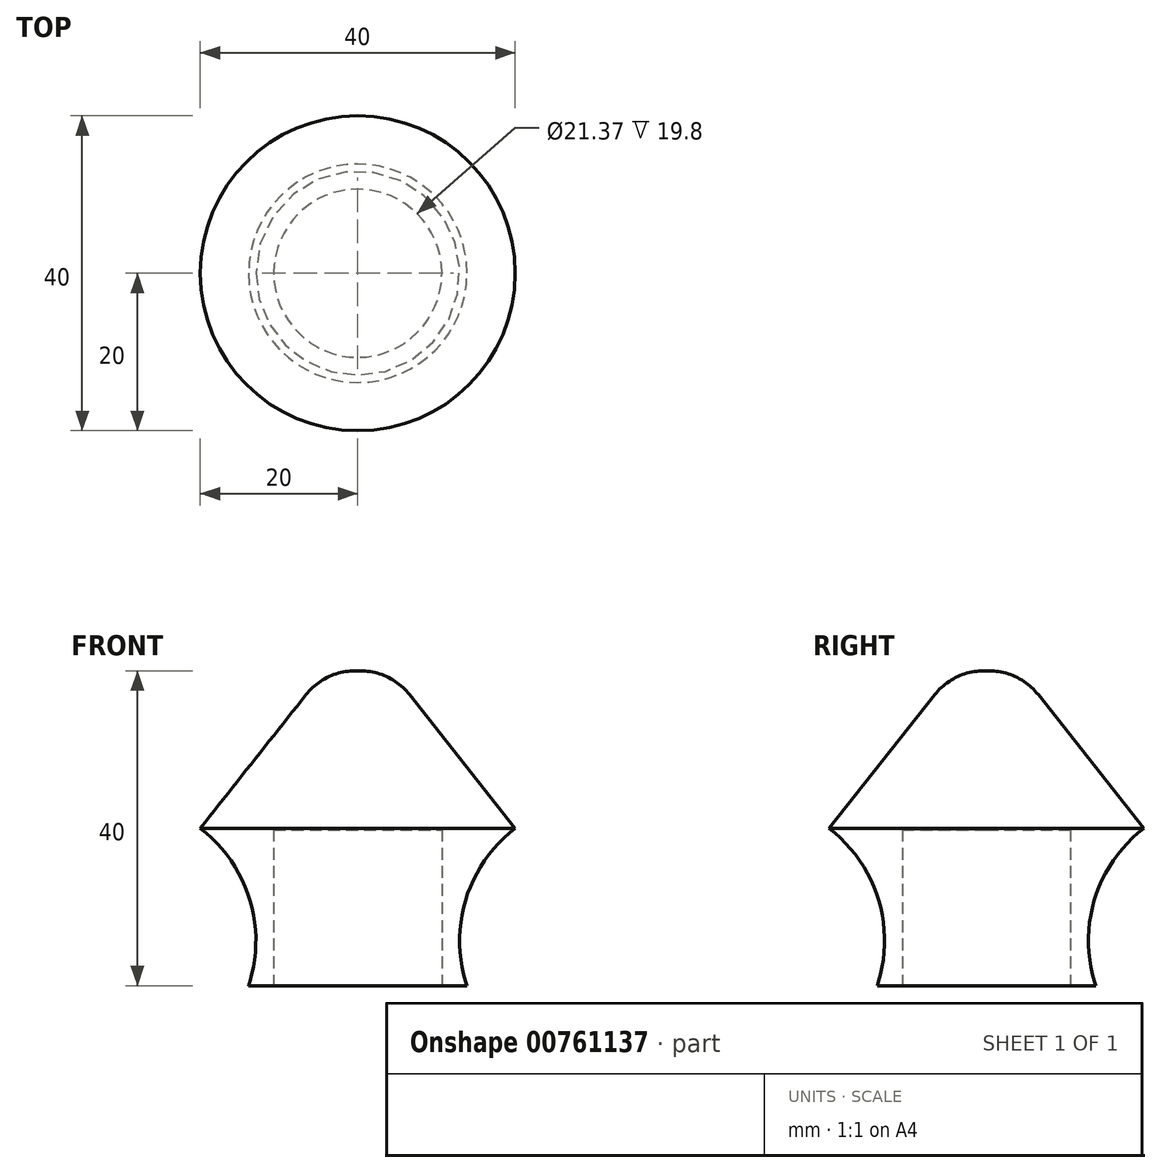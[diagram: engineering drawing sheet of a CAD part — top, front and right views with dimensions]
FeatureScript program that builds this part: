
annotation { "Feature Type Name" : "Feature", "Feature Type Description" : "" }
export const myFeature = defineFeature(function(context is Context, id is Id, definition is map)
    precondition{}
    {
        {
            var Q0;
            Q0=qCreatedBy(makeId("Front.planeOp"),FACE);
            var sketch = newSketch(context, id + "F0", { "sketchPlane" : qUnion([Q0])});
            skLineSegment(sketch, "E0.bottom", {"start": v(-4.17, 20) * mm, "end": v(0, 20) * mm});
            skLineSegment(sketch, "E0.top", {"start": v(-13.87, -20) * mm, "end": v(0, -20) * mm});
            skPoint(sketch, "E0.middle", {"position": v(0, 0) * mm});
            skLineSegment(sketch, "E1", {"start": v(0, 29.23) * mm, "end": v(0, -32.46) * mm});
            skLineSegment(sketch, "E2", {"start": v(-4.17, 20) * mm, "end": v(-20, 0) * mm});
            skLineSegment(sketch, "E3", {"start": v(-20, 0) * mm, "end": v(-7.86, 0) * mm});
            skLineSegment(sketch, "E4", {"start": v(-7.86, 0) * mm, "end": v(-13.87, -20) * mm});
            skPoint(sketch, "E0.right.start.orphan", {"position": v(20, 20) * mm});
            skPoint(sketch, "E5.orphan", {"position": v(20, -20) * mm});
            skPoint(sketch, "E6.orphan", {"position": v(-20, -20) * mm});
            skPoint(sketch, "E7.orphan", {"position": v(-20, 20) * mm});
            skSolve(sketch);
        }
        {
            var Q0;
            Q0 = qSketchRegion(id + "F0", true);
            var Q1;
            Q1=sQuery(id+"F0.wireOp",EDGE,"E1");
            revolve(context, id + "F1", {"surfaceOperationType" : NewSurfaceOperationType.NEW, "entities" : qUnion([Q0]), "axis" : qUnion([Q1]), "revolveType" : RevolveType.FULL});
        }
        {
            var Q0;
            Q0=makeQuery(id+"F1.opRevolve","SWEPT_EDGE",EDGE,{"disambiguationData":[OSD([sQuery(id+"F0.wireOp",EDGE,"E3"),sQuery(id+"F0.wireOp",EDGE,"E4")])]});
            fillet(context, id + "F2", {"entities" : qUnion([Q0]), "radius" : 18 * mm, "tangentPropagation" : true, "allowEdgeOverflow" : false});
        }
        {
            var Q0;
            Q0=makeQuery(id+"F1.opRevolve","SWEPT_EDGE",EDGE,{"disambiguationData":[OSD([sQuery(id+"F0.wireOp",EDGE,"E0.bottom"),sQuery(id+"F0.wireOp",EDGE,"E2")])]});
            fillet(context, id + "F3", {"entities" : qUnion([Q0]), "radius" : 8 * mm, "tangentPropagation" : true, "allowEdgeOverflow" : false});
        }
        {
            var Q0;
            Q0=makeQuery(id+"F1.opRevolve","SWEPT_FACE",FACE,{"disambiguationData":[OSD([sQuery(id+"F0.wireOp",EDGE,"E0.top")])]});
            var sketch = newSketch(context, id + "F4", { "sketchPlane" : qUnion([Q0])});
            skCircle(sketch, "E8", {"center": v(0, 0) * mm, "radius": 10.68 * mm});
            skSolve(sketch);
        }
        {
            var Q0;
            Q0 = qSketchRegion(id + "F4", true);
            extrude(context, id + "F5", {"entities" : qUnion([Q0]), "operationType" : NewBodyOperationType.REMOVE, "oppositeDirection" : true, "depth" : 19.8 * mm, "offsetDistance" : 25 * mm});
        }
    });
